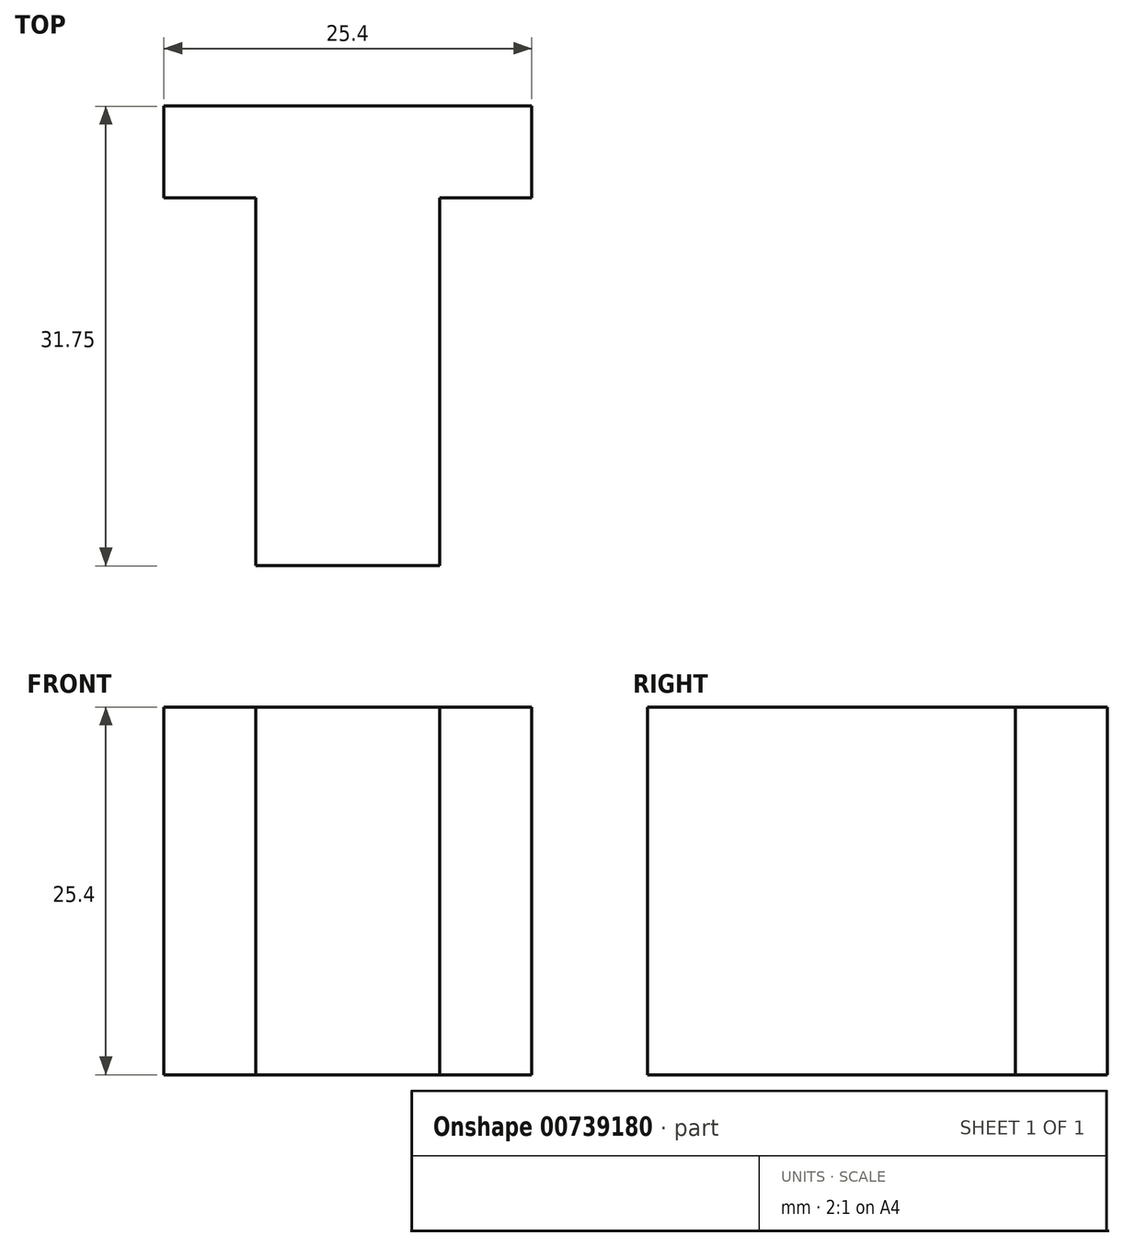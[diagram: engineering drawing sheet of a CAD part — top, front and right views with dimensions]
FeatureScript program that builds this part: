
annotation { "Feature Type Name" : "Feature", "Feature Type Description" : "" }
export const myFeature = defineFeature(function(context is Context, id is Id, definition is map)
    precondition{}
    {
        {
            var Q0;
            Q0=qCreatedBy(makeId("Top.planeOp"),FACE);
            var sketch = newSketch(context, id + "F0", { "sketchPlane" : qUnion([Q0])});
            skLineSegment(sketch, "E0", {"start": v(0, 19.81) * mm, "end": v(0, -11.94) * mm});
            skLineSegment(sketch, "E1", {"start": v(0, -11.94) * mm, "end": v(25.4, -11.94) * mm});
            skLineSegment(sketch, "E2", {"start": v(25.4, -11.94) * mm, "end": v(25.4, 19.81) * mm});
            skLineSegment(sketch, "E3", {"start": v(25.4, 19.81) * mm, "end": v(0, 19.81) * mm});
            skSolve(sketch);
        }
        {
            var Q0;
            Q0=makeQuery(id+"F0.imprint","IMPRINT",FACE,{"disambiguationData":[TD([[makeQuery(id+"F0.imprint","IMPRINT",EDGE,{"derivedFrom":sQuery(id+"F0.wireOp",EDGE,"E0")}),1.0]])]});
            extrude(context, id + "F1", {"entities" : qUnion([Q0]), "depth" : 25.4 * mm, "offsetDistance" : 25.4 * mm});
        }
        {
            var Q0;
            Q0=makeQuery(id+"F1.opExtrude","CAP_FACE",FACE,{"disambiguationData":[OSD([sQuery(id+"F0.wireOp",EDGE,"E0"),sQuery(id+"F0.wireOp",EDGE,"E1"),sQuery(id+"F0.wireOp",EDGE,"E2"),sQuery(id+"F0.wireOp",EDGE,"E3")])],"isStart":false});
            var sketch = newSketch(context, id + "F2", { "sketchPlane" : qUnion([Q0])});
            skLineSegment(sketch, "E4", {"start": v(0, 13.46) * mm, "end": v(6.35, 13.46) * mm});
            skLineSegment(sketch, "E5", {"start": v(6.35, 13.46) * mm, "end": v(6.35, -11.94) * mm});
            skPoint(sketch, "E5.endSnap0", {"position": v(12.7, -11.94) * mm});
            skSolve(sketch);
        }
        {
            var Q0;
            {var subQ0=sQuery(id+"F2.wireOp",EDGE,"E4");Q0=makeQuery(id+"F2.imprint","IMPRINT",FACE,{"disambiguationData":[TD([[makeQuery(id+"F2.imprint","IMPRINT",EDGE,{"derivedFrom":subQ0}),-1.0]])]});}
            extrude(context, id + "F3", {"entities" : qUnion([Q0]), "operationType" : NewBodyOperationType.REMOVE, "endBound" : BoundingType.THROUGH_ALL, "oppositeDirection" : true, "depth" : 25.4 * mm, "offsetDistance" : 25.4 * mm});
        }
        {
            var Q0;
            Q0=makeQuery(id+"F1.opExtrude","CAP_FACE",FACE,{"disambiguationData":[OSD([sQuery(id+"F0.wireOp",EDGE,"E0"),sQuery(id+"F0.wireOp",EDGE,"E1"),sQuery(id+"F0.wireOp",EDGE,"E2"),sQuery(id+"F0.wireOp",EDGE,"E3")])],"isStart":false});
            var sketch = newSketch(context, id + "F4", { "sketchPlane" : qUnion([Q0])});
            skLineSegment(sketch, "E6", {"start": v(25.4, 13.46) * mm, "end": v(19.05, 13.46) * mm});
            skLineSegment(sketch, "E7", {"start": v(19.05, 13.46) * mm, "end": v(19.05, -11.94) * mm});
            skSolve(sketch);
        }
        {
            var Q0;
            {var subQ0=sQuery(id+"F4.wireOp",EDGE,"E6");Q0=makeQuery(id+"F4.imprint","IMPRINT",FACE,{"disambiguationData":[TD([[makeQuery(id+"F4.imprint","IMPRINT",EDGE,{"derivedFrom":subQ0}),1.0]])]});}
            extrude(context, id + "F5", {"entities" : qUnion([Q0]), "operationType" : NewBodyOperationType.REMOVE, "endBound" : BoundingType.THROUGH_ALL, "oppositeDirection" : true, "depth" : 25.4 * mm, "offsetDistance" : 25.4 * mm});
        }
    });
